# Revit family: Partition-7_Panels_High-Skyfold_Classic_Compact-12-1_to_14-0_FC_3680_to_4265
name_source: partatom
category: Generic Models
units: mm (PartAtom-declared; Revit-internal decimal feet)

## family parameters
Always vertical = Yes
Can host rebar = No
Cut with Voids When Loaded = No
Host = Ceiling
Maintain Annotation Orientation = No
Part Type = Normal
Room Calculation Point = No
Round Connector Dimension = Use Diameter
Shared = No

## types (5) — shared parameters
Default Elevation = 0' - 0"
Distance From Acoustic Barrier = 0' - 2"
Manufacturer = Skyfold
Model = Compact Drive System
URL = http://www.skyfold.com
http://www.skyfold.com
http://www.skyfold.com
http://www.skyfold.com
Wall Thickness = 0' - 11 3/4"

## per-type parameters (varying)
| type | Acoustic Barrier"C" | Beam Height"B" | Description | Panel Height"F" | Pocket Depth"D" | Pocket Width"E" | Total Panel Height |
| 12' - 6" | 14' - 7" | 15' - 7 1/2" | Custom Powerlift Partitions | 2' - 0" | 2' - 2" | 4' - 10 3/4" | 14' - 3" |
| 13' - 6" | 15' - 7 1/4" | 16' - 7 3/4" | Custom Powerlift Partitions
Custom Powerlift Partitions
Custom Powerlift Partitions
Custom Powerlift Partitions
Custom Powerlift Partitions | 2' - 1 3/4" | 2' - 2 1/4" | 5' - 2 1/4" | 15' - 3 1/4" |
| 12' - 1" | 14' - 1 3/4" | 15' - 2 1/4" | Custom Powerlift Partitions | 1' - 11 1/4" | 2' - 1 3/4" | 4' - 9 1/4" | 13' - 9 3/4" |
| 13' - 0" | 15' - 0 1/4" | 16' - 0 3/4" | Custom Powerlift Partitions | 2' - 0 3/4" | 2' - 1 1/4" | 5' - 0 1/4" | 14' - 8 1/4" |
| 14' - 0" | 16' - 0 1/2" | 17' - 1" | Custom Powerlift Partitions | 2' - 2 1/2" | 2' - 1 1/2" | 5' - 3 3/4" | 15' - 8 1/2" |

note: column(s) folded — value = type name in every type: Finished Ceiling"A"

## geometry (parser evidence)
native form markers: Sweep x24
no freeform markers — native parametric forms only
